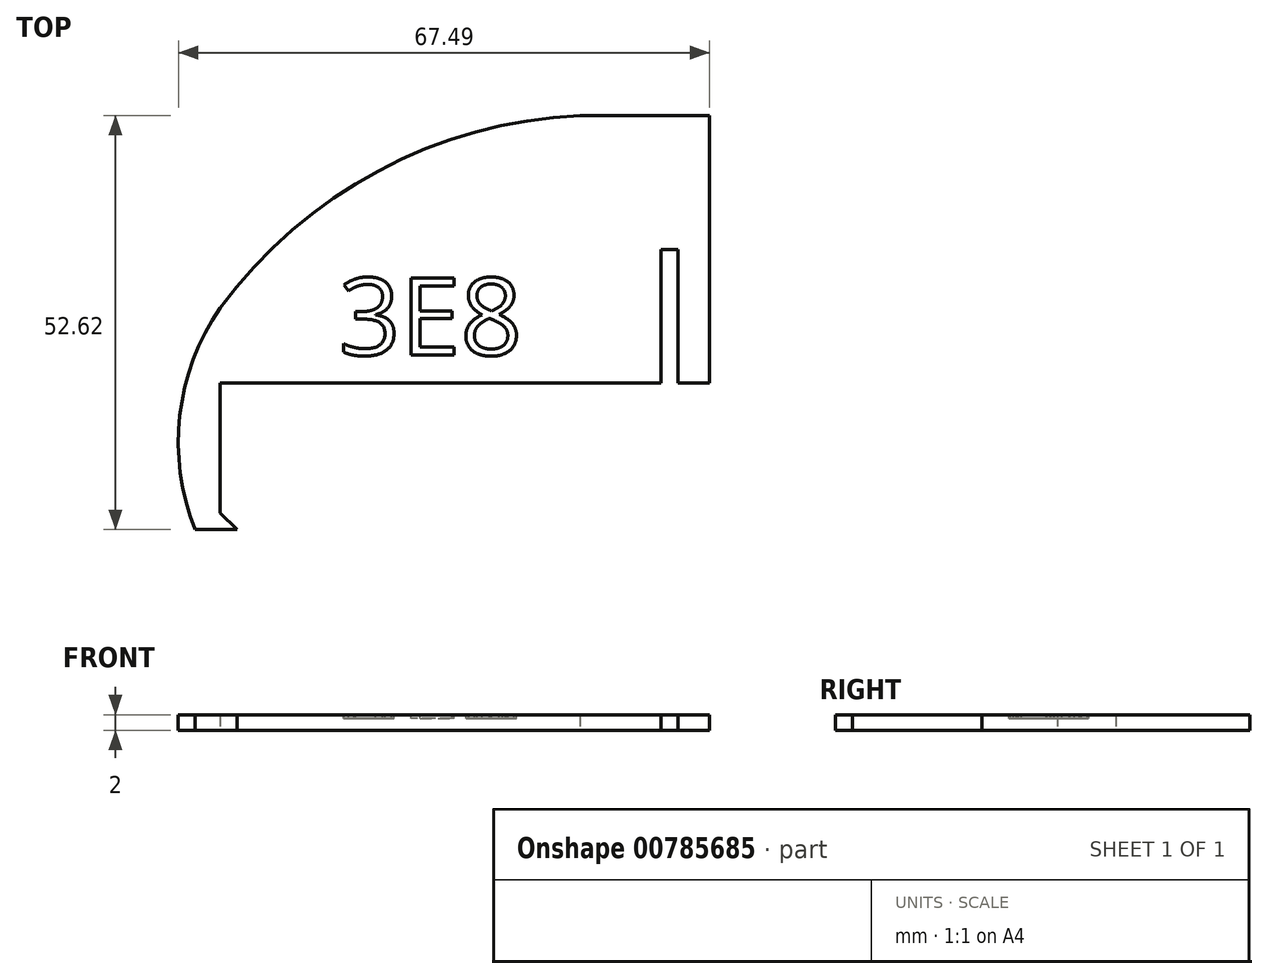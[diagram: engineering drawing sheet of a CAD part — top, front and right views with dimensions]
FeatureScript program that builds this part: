
annotation { "Feature Type Name" : "Feature", "Feature Type Description" : "" }
export const myFeature = defineFeature(function(context is Context, id is Id, definition is map)
    precondition{}
    {
        {
            assignVariable(context, id + "F0", {"name" : "slatthickness", "anyValue" : 2});
        }
        {
            var Q0;
            Q0=qCreatedBy(makeId("Top.planeOp"),FACE);
            var sketch = newSketch(context, id + "F1", { "sketchPlane" : qUnion([Q0])});
            skLineSegment(sketch, "E0", {"start": v(-35, 0) * mm, "end": v(35, 0) * mm, "construction": true});
            skLineSegment(sketch, "E1", {"start": v(0, 9.87) * mm, "end": v(0, -24.13) * mm, "construction": true});
            skLineSegment(sketch, "E2.bottom", {"start": v(-64.03, 9.87) * mm, "end": v(64.03, 9.87) * mm, "construction": true});
            skLineSegment(sketch, "E2.top", {"start": v(-64.03, -24.13) * mm, "end": v(64.03, -24.13) * mm, "construction": true});
            skLineSegment(sketch, "E2.right", {"start": v(64.03, 9.87) * mm, "end": v(64.03, -24.13) * mm, "construction": true});
            skLineSegment(sketch, "E3.MirrorCS", {"start": v(30.8, -4.86) * mm, "end": v(39.2, -4.86) * mm, "construction": true});
            skLineSegment(sketch, "E4.MirrorCS", {"start": v(30.8, 4.86) * mm, "end": v(30.8, -4.86) * mm, "construction": true});
            skLineSegment(sketch, "E5.MirrorCS", {"start": v(30.8, 4.86) * mm, "end": v(39.2, 4.86) * mm, "construction": true});
            skLineSegment(sketch, "E6.MirrorCS", {"start": v(39.2, 4.86) * mm, "end": v(39.2, -4.86) * mm, "construction": true});
            skLineSegment(sketch, "E7.MirrorCS", {"start": v(54.85, 4.86) * mm, "end": v(54.85, -4.86) * mm, "construction": true});
            skLineSegment(sketch, "E8.MirrorCS", {"start": v(54.85, 4.86) * mm, "end": v(63.25, 4.86) * mm, "construction": true});
            skLineSegment(sketch, "E9.MirrorCS", {"start": v(63.25, 4.86) * mm, "end": v(63.25, -4.86) * mm, "construction": true});
            skLineSegment(sketch, "E10.MirrorCS", {"start": v(54.85, -4.86) * mm, "end": v(63.25, -4.86) * mm, "construction": true});
            skLineSegment(sketch, "E11", {"start": v(-4.93, -7.13) * mm, "end": v(4.94, -7.13) * mm, "construction": true});
            skLineSegment(sketch, "E12.MirrorCS", {"start": v(4.93, -7.13) * mm, "end": v(4.94, 9.87) * mm, "construction": true});
            skLineSegment(sketch, "E13.MirrorCS", {"start": v(4.93, -7.13) * mm, "end": v(7.08, -7.13) * mm, "construction": true});
            skLineSegment(sketch, "E14.MirrorCS", {"start": v(7.08, -7.13) * mm, "end": v(7.08, 9.87) * mm, "construction": true});
            skSolve(sketch);
        }
        {
            var Q0;
            Q0=qCreatedBy(makeId("Top.planeOp"),FACE);
            var sketch = newSketch(context, id + "F2", { "sketchPlane" : qUnion([Q0])});
            skPoint(sketch, "E15.0", {"position": v(4.94, -7.13) * mm});
            skPoint(sketch, "E16.0", {"position": v(7.08, -7.13) * mm});
            skPoint(sketch, "E17.0", {"position": v(0, -24.13) * mm});
            skPoint(sketch, "E18.0", {"position": v(0, 9.87) * mm});
            skPoint(sketch, "E19.0", {"position": v(30.8, -4.86) * mm});
            skLineSegment(sketch, "E20.bottom", {"start": v(4.94, -7.13) * mm, "end": v(7.08, -7.13) * mm});
            skLineSegment(sketch, "E20.top", {"start": v(4.94, -24.13) * mm, "end": v(7.08, -24.13) * mm});
            skLineSegment(sketch, "E20.left", {"start": v(4.94, -7.13) * mm, "end": v(4.94, -24.13) * mm});
            skLineSegment(sketch, "E20.right", {"start": v(7.08, -7.13) * mm, "end": v(7.08, -24.13) * mm});
            skLineSegment(sketch, "E21.bottom", {"start": v(11.08, -24.13) * mm, "end": v(-51.06, -24.13) * mm});
            skLineSegment(sketch, "E21.top", {"start": v(11.08, 9.87) * mm, "end": v(-51.06, 9.87) * mm});
            skLineSegment(sketch, "E21.left", {"start": v(11.08, -24.13) * mm, "end": v(11.08, 9.87) * mm});
            skLineSegment(sketch, "E21.right", {"start": v(-51.06, -24.13) * mm, "end": v(-51.06, 9.87) * mm});
            skLineSegment(sketch, "E22", {"start": v(30.8, -4.86) * mm, "end": v(30.8, -19.7) * mm, "construction": true});
            skLineSegment(sketch, "E23", {"start": v(-51.06, -24.13) * mm, "end": v(-51.06, -40.63) * mm});
            skLineSegment(sketch, "E24", {"start": v(-51.06, -40.63) * mm, "end": v(-48.94, -42.75) * mm});
            skLineSegment(sketch, "E25", {"start": v(-48.94, -42.75) * mm, "end": v(-54.28, -42.75) * mm});
            skArc(sketch, "E26", {"start": v(-51.07, -14.58) * mm, "mid": v(-56.21, -28.26) * mm, "end": v(-54.28, -42.75) * mm});
            skArc(sketch, "E27", {"start": v(0, 9.87) * mm, "mid": v(-28.6, 4.05) * mm, "end": v(-51.06, -14.58) * mm});
            skSolve(sketch);
        }
        {
            var Q0;
            Q0=makeQuery(id+"F2.imprint","IMPRINT",FACE,{"disambiguationData":[TD([[makeQuery(id+"F2.imprint","IMPRINT",EDGE,{"derivedFrom":sQuery(id+"F2.wireOp",EDGE,"E20.bottom")}),1.0]])]});
            var Q1;
            {var subQ0=sQuery(id+"F2.wireOp",EDGE,"E23");Q1=makeQuery(id+"F2.imprint","IMPRINT",FACE,{"disambiguationData":[TD([[makeQuery(id+"F2.imprint","IMPRINT",EDGE,{"derivedFrom":subQ0}),-1.0]])]});}
            extrude(context, id + "F3", {"entities" : qUnion([Q0, Q1]), "depth" : (getVariable(context, 'slatthickness')) * mm, "offsetDistance" : 25 * mm});
        }
        {
            var Q0;
            Q0=makeQuery(id+"F3.opExtrude","CAP_FACE",FACE,{"disambiguationData":[OSD([sQuery(id+"F2.wireOp",EDGE,"E20.bottom"),sQuery(id+"F2.wireOp",EDGE,"E20.left"),sQuery(id+"F2.wireOp",EDGE,"E20.right"),sQuery(id+"F2.wireOp",EDGE,"E21.bottom"),sQuery(id+"F2.wireOp",EDGE,"E21.top"),sQuery(id+"F2.wireOp",EDGE,"E21.left"),sQuery(id+"F2.wireOp",EDGE,"E23"),sQuery(id+"F2.wireOp",EDGE,"E24"),sQuery(id+"F2.wireOp",EDGE,"E25"),sQuery(id+"F2.wireOp",EDGE,"E26"),sQuery(id+"F2.wireOp",EDGE,"E27")])],"isStart":false});
            var sketch = newSketch(context, id + "F4", { "sketchPlane" : qUnion([Q0])});
            skText(sketch, "E28", { "text": "3E8", "fontName": "OpenSans-Regular.ttf"});
            skLineSegment(sketch, "E29", {"start": v(4.94, -15.63) * mm, "end": v(-24.3, -15.63) * mm, "construction": true});
            const initialGuessF4  = {"E28": [-0.03604, -0.02057, 1, 0, 0.00987]};
            skSetInitialGuess(sketch, initialGuessF4);
            skSolve(sketch);
        }
        {
            var Q0;
            Q0 = qSketchRegion(id + "F4", true);
            extrude(context, id + "F5", {"entities" : qUnion([Q0]), "operationType" : NewBodyOperationType.REMOVE, "oppositeDirection" : true, "depth" : .5 * mm, "offsetDistance" : 25 * mm});
        }
    });
